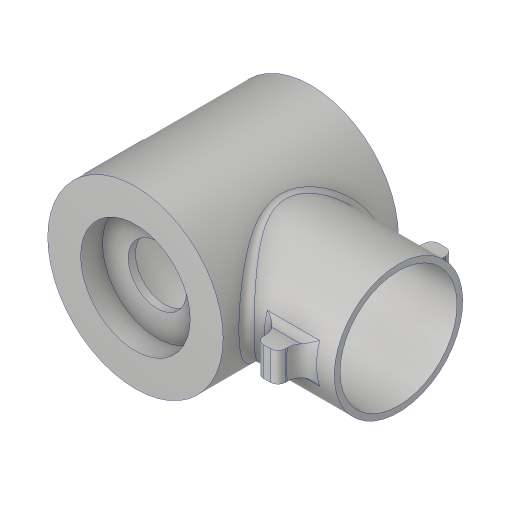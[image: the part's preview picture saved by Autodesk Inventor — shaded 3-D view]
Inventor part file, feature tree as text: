
AUTODESK INVENTOR PART (.ipt)
format: ipt  version: 2023.4 (Build 274418000, 418)  size: 350,208 bytes
history: native  units: in
note: dims shown in document units (in); Inventor stores cm internally (conversion verified against a paired STEP export)
features: sketch x8, extrude x6, plane x3, hole x2, fillet x2, mirror x1
ambient origin geometry x8: Origin, YZ Plane, XZ Plane, XY Plane, X Axis, Y Axis, Z Axis, Center Point
bodies: Solid1 (feature_tree)
feature tree (22):
  extrude  "Extrusion1"  Depth=3.0in TaperAngle=0.0deg
  plane  "Work Plane1"
  extrude  "Extrusion2"  Depth=2.0in
  extrude  "Extrusion3"  Depth=3.0in TaperAngle=0.0deg
  hole  "Hole1"  [1 undecoded]
  plane  "Work Plane2"
  extrude  "Extrusion4"  Depth=0.5in
  mirror  "Mirror1"
  plane  "Work Plane3"
  extrude  "Extrusion5"  [1 undecoded]
  fillet  "Fillet1"  Radius=0.5in
  fillet  "Fillet2"  Radius=1.25in
  hole  "Hole2"  [1 undecoded]
  extrude  "Extrusion6"  Depth=2.0in
  sketch  "Sketch1"  dims[d0=3.0in d1=3.0in d2=0.0in]
  sketch  "Sketch2"  dims[d3=3.0in d4=2.0in]
  sketch  "Sketch3"  dims[d5=0.1in d6=3.0in d7=0.0in]
  sketch  "Sketch4"  dims[d8=3.3in d9=0.0in]
  sketch  "Sketch6"  dims[d11=1.0in d12=0.75in d13=1.875in d14=0.375in d15=0.5635in d16=1.625in d17=0.8108in d22=1.5in]
  sketch  "Sketch7"  dims[d23=0.375in d24=0.5in]
  sketch  "Sketch8"  dims[d25=0.5in d26=0.0in d27=-1.875in d28=0.5in d29=1.25in]
  sketch  "Sketch9"  dims[d30=1.0in d31=0.0in d32=0.26in d33=0.13in d34=0.9in d35=0.75in d36=1.875in d37=0.375in d38=0.5635in d39=1.0in d40=0.8108in d41=2.0in d42=0.0in d43=0.5in d44=0.0344in d45=0.5in d46=0.0344in]
note: 3 required parameter values undecoded (feature->parameter linkage not recoverable at this tier; creation-order binding heuristic only, values carry confidence <= 0.55)
